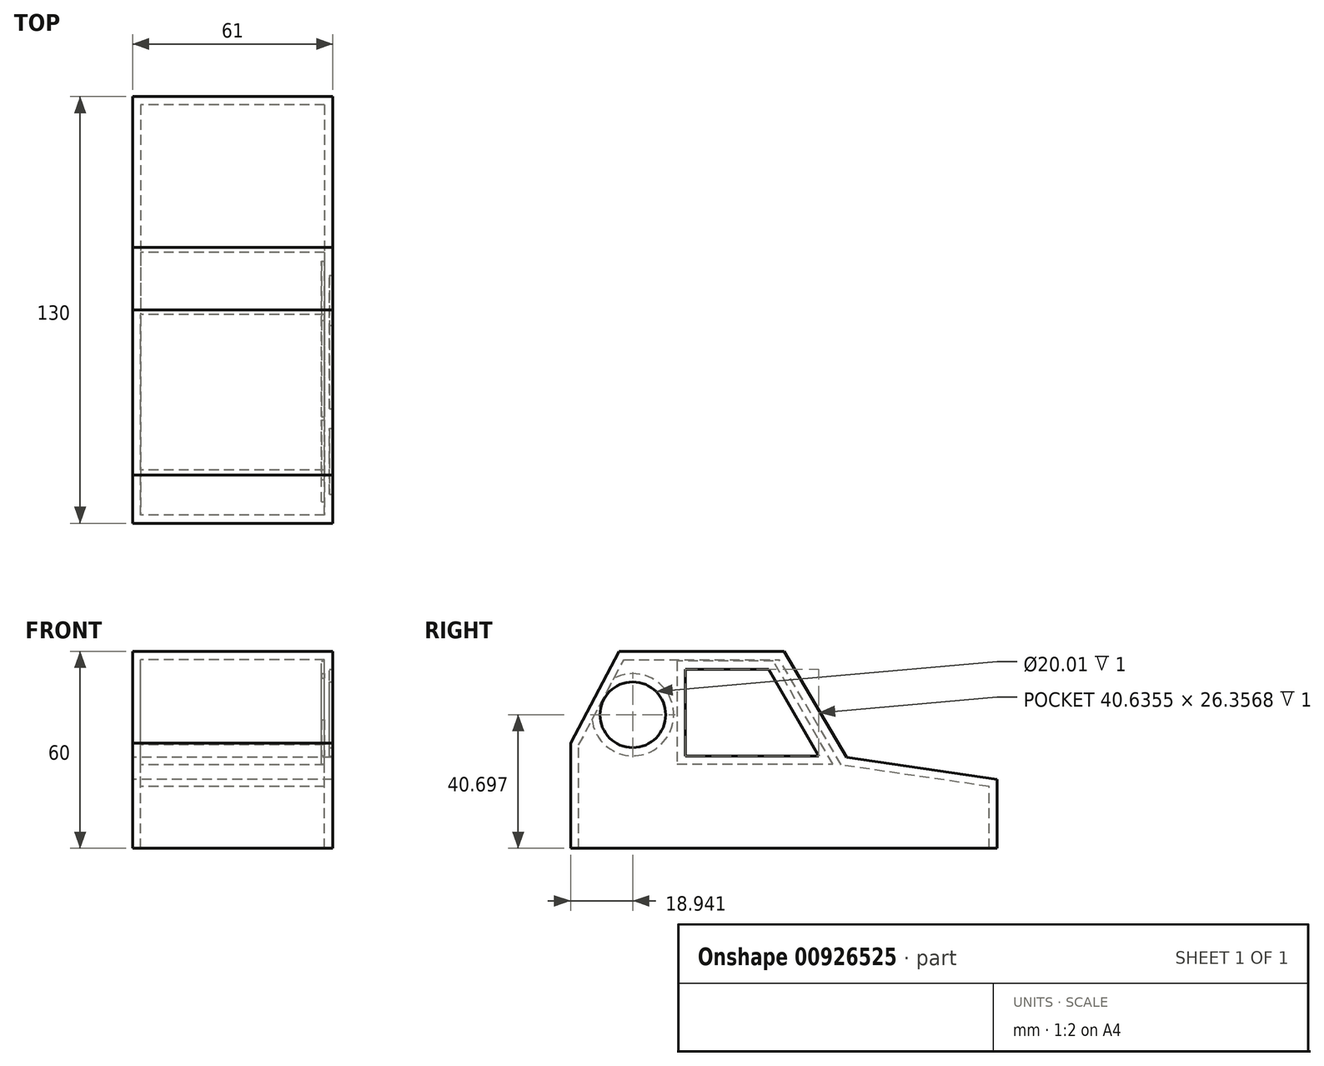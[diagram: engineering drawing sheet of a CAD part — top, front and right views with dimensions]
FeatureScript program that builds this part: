
annotation { "Feature Type Name" : "Feature", "Feature Type Description" : "" }
export const myFeature = defineFeature(function(context is Context, id is Id, definition is map)
    precondition{}
    {
        {
            var Q0;
            Q0=qCreatedBy(makeId("Right.planeOp"),FACE);
            var sketch = newSketch(context, id + "F0", { "sketchPlane" : qUnion([Q0])});
            skLineSegment(sketch, "E0.bottom", {"start": v(-60.36, 0) * mm, "end": v(-47.56, 0) * mm});
            skLineSegment(sketch, "E0.top", {"start": v(-45.59, 60) * mm, "end": v(4.64, 60) * mm});
            skLineSegment(sketch, "E0.left", {"start": v(-60.36, 0) * mm, "end": v(-60.36, 32.11) * mm});
            skLineSegment(sketch, "E0.right", {"start": v(69.64, 0) * mm, "end": v(69.64, 21) * mm});
            skLineSegment(sketch, "E1", {"start": v(-60.36, 32.11) * mm, "end": v(-45.59, 60) * mm});
            skLineSegment(sketch, "E2", {"start": v(69.64, 21) * mm, "end": v(23.69, 27.69) * mm});
            skLineSegment(sketch, "E3", {"start": v(23.69, 27.69) * mm, "end": v(4.64, 60) * mm});
            skArc(sketch, "E4", {"start": v(-22.56, 0) * mm, "mid": v(-35.06, 12.5) * mm, "end": v(-47.56, 0) * mm});
            skArc(sketch, "E5", {"start": v(54.09, 0) * mm, "mid": v(41.59, 12.5) * mm, "end": v(29.09, 0) * mm});
            skPoint(sketch, "E6.orphan", {"position": v(-60.36, 60) * mm});
            skPoint(sketch, "E7.orphan", {"position": v(69.64, 60) * mm});
            skLineSegment(sketch, "E8.trimOffspring", {"start": v(54.09, 0) * mm, "end": v(69.64, 0) * mm});
            skLineSegment(sketch, "E9.trimOffspring", {"start": v(-22.56, 0) * mm, "end": v(29.09, 0) * mm});
            skLineSegment(sketch, "E10", {"start": v(54.09, 0) * mm, "end": v(29.09, 0) * mm});
            skLineSegment(sketch, "E11", {"start": v(-22.56, 0) * mm, "end": v(-47.56, 0) * mm});
            skSolve(sketch);
        }
        {
            var Q0;
            Q0 = qSketchRegion(id + "F0", true);
            extrude(context, id + "F1", {"entities" : qUnion([Q0]), "depth" : 61 * mm, "offsetDistance" : 25 * mm, "symmetric" : true});
        }
        {
            var Q0;
            Q0=qCreatedBy(makeId("Front.planeOp"),FACE);
            var sketch = newSketch(context, id + "F2", { "sketchPlane" : qUnion([Q0])});
            skFitSpline(sketch, "E12", {"points": [v(26.39, 60.9) * mm, v(30.2, 33.98) * mm, v(27.7, -1.63) * mm], "startDerivative": vector(11.18, -55.69) * mm, "endDerivative": vector(-8.12, -69.08) * mm});
            skLineSegment(sketch, "E13", {"start": v(26.39, 60.9) * mm, "end": v(45.32, 60.9) * mm});
            skLineSegment(sketch, "E14", {"start": v(45.32, 60.9) * mm, "end": v(42.58, -2) * mm});
            skLineSegment(sketch, "E15", {"start": v(42.58, -2) * mm, "end": v(27.7, -1.63) * mm});
            skLineSegment(sketch, "E16.MirrorCS", {"start": v(-26.39, 60.9) * mm, "end": v(-45.32, 60.9) * mm});
            skFitSpline(sketch, "E17.MirrorCS", {"points": [v(-26.39, 60.9) * mm, v(-30.2, 33.98) * mm, v(-27.7, -1.63) * mm], "startDerivative": vector(-11.18, -55.69) * mm, "endDerivative": vector(8.12, -69.08) * mm});
            skLineSegment(sketch, "E18.MirrorCS", {"start": v(-42.58, -2) * mm, "end": v(-27.7, -1.63) * mm});
            skLineSegment(sketch, "E19.MirrorCS", {"start": v(-45.32, 60.9) * mm, "end": v(-42.58, -2) * mm});
            skSolve(sketch);
        }
        {
            var Q0;
            Q0=makeQuery(id+"F1.opExtrude","CAP_FACE",FACE,{"disambiguationData":[OSD([sQuery(id+"F0.wireOp",EDGE,"E0.bottom"),sQuery(id+"F0.wireOp",EDGE,"E0.top"),sQuery(id+"F0.wireOp",EDGE,"E0.left"),sQuery(id+"F0.wireOp",EDGE,"E0.right"),sQuery(id+"F0.wireOp",EDGE,"E1"),sQuery(id+"F0.wireOp",EDGE,"E2"),sQuery(id+"F0.wireOp",EDGE,"E3"),sQuery(id+"F0.wireOp",EDGE,"E4"),sQuery(id+"F0.wireOp",EDGE,"E5"),sQuery(id+"F0.wireOp",EDGE,"E8.trimOffspring"),sQuery(id+"F0.wireOp",EDGE,"E9.trimOffspring")])],"isStart":false});
            var sketch = newSketch(context, id + "F3", { "sketchPlane" : qUnion([Q0])});
            skLineSegment(sketch, "E20", {"start": v(15.23, 28.15) * mm, "end": v(0, 54.51) * mm});
            skLineSegment(sketch, "E21", {"start": v(0, 54.51) * mm, "end": v(-25.4, 54.51) * mm});
            skLineSegment(sketch, "E22", {"start": v(-25.4, 54.51) * mm, "end": v(-25.4, 28.15) * mm});
            skLineSegment(sketch, "E23", {"start": v(-25.4, 28.15) * mm, "end": v(15.23, 28.15) * mm});
            skCircle(sketch, "E24", {"center": v(-41.42, 40.7) * mm, "radius": 10 * mm});
            skSolve(sketch);
        }
        {
            var Q0;
            Q0 = qSketchRegion(id + "F3", true);
            extrude(context, id + "F4", {"entities" : qUnion([Q0]), "operationType" : NewBodyOperationType.REMOVE, "oppositeDirection" : true, "depth" : 1 * mm, "offsetDistance" : 25 * mm});
        }
        {
            var Q0;
            Q0=makeQuery(id+"F1.opExtrude","SWEPT_FACE",FACE,{"disambiguationData":[OSD([sQuery(id+"F0.wireOp",EDGE,"E0.bottom"),sQuery(id+"F0.wireOp",EDGE,"E8.trimOffspring"),sQuery(id+"F0.wireOp",EDGE,"E9.trimOffspring"),sQuery(id+"F0.wireOp",EDGE,"E10"),sQuery(id+"F0.wireOp",EDGE,"E11")])]});
            shell(context, id + "F5", {"entities" : qUnion([Q0]), "thickness" : 2.5 * mm});
        }
        {
            var Q0;
            Q0=makeQuery(id+"F0.imprint","IMPRINT",FACE,{"disambiguationData":[TD([[makeQuery(id+"F0.imprint","IMPRINT",EDGE,{"derivedFrom":sQuery(id+"F0.wireOp",EDGE,"E5")}),1.0]])]});
            var Q1;
            Q1=makeQuery(id+"F0.imprint","IMPRINT",FACE,{"disambiguationData":[TD([[makeQuery(id+"F0.imprint","IMPRINT",EDGE,{"derivedFrom":sQuery(id+"F0.wireOp",EDGE,"E4")}),1.0]])]});
            extrude(context, id + "F6", {"entities" : qUnion([Q0, Q1]), "operationType" : NewBodyOperationType.REMOVE, "depth" : 25 * mm, "offsetDistance" : 25 * mm, "hasSecondDirection" : true, "secondDirectionBound" : BoundingType.THROUGH_ALL, "secondDirectionOppositeDirection" : true, "secondDirectionDepth" : 25 * mm, "symmetric" : true});
        }
    });
